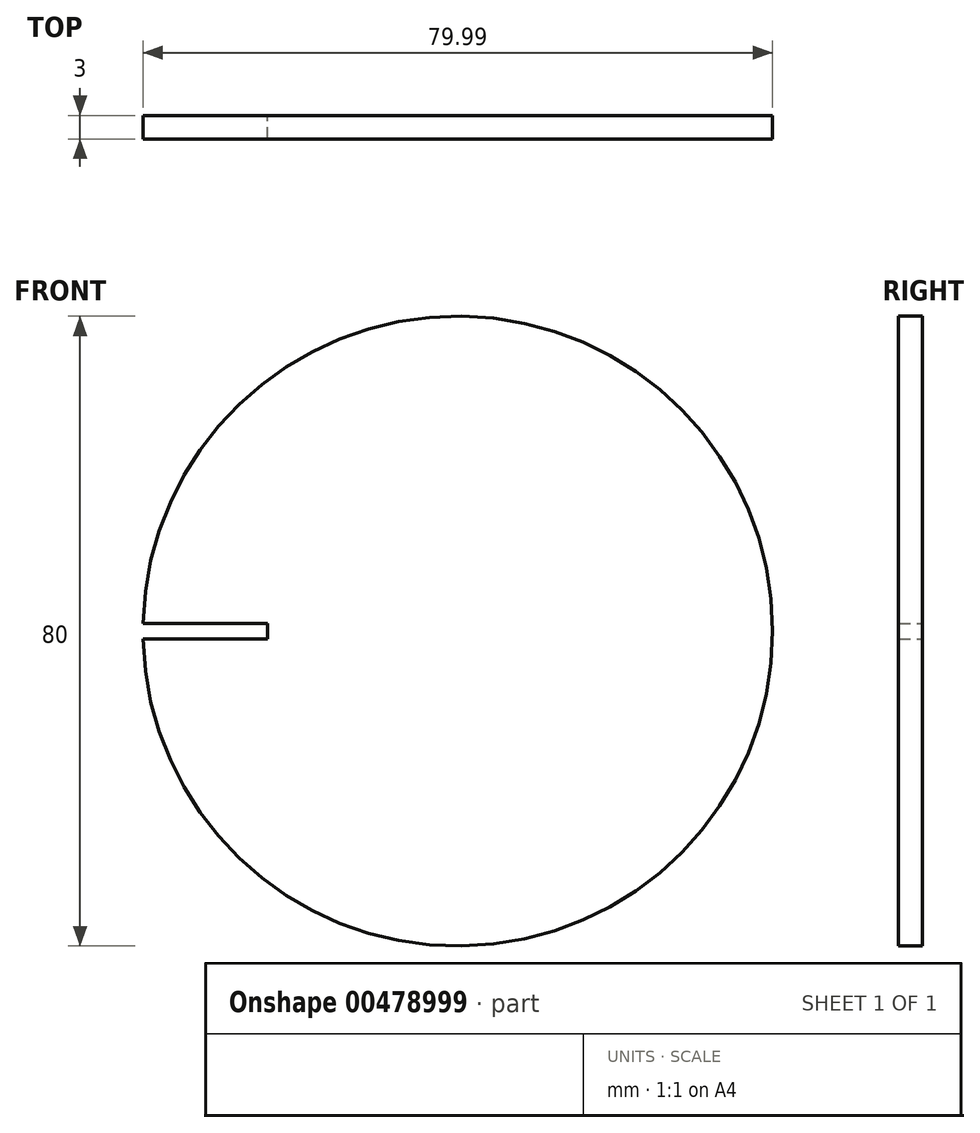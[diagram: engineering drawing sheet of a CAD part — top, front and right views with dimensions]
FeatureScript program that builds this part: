
annotation { "Feature Type Name" : "Feature", "Feature Type Description" : "" }
export const myFeature = defineFeature(function(context is Context, id is Id, definition is map)
    precondition{}
    {
        {
            var Q0;
            Q0=qCreatedBy(makeId("Front.planeOp"),FACE);
            var sketch = newSketch(context, id + "F0", { "sketchPlane" : qUnion([Q0])});
            skCircle(sketch, "E0", {"center": v(0, 0) * mm, "radius": 40 * mm});
            skSolve(sketch);
        }
        {
            var Q0;
            Q0=makeQuery(id+"F0.imprint","IMPRINT",FACE,{"disambiguationData":[TD([[makeQuery(id+"F0.imprint","IMPRINT",EDGE,{"derivedFrom":sQuery(id+"F0.wireOp",EDGE,"E0")}),1.0]])]});
            extrude(context, id + "F1", {"entities" : qUnion([Q0]), "depth" : 3 * mm});
        }
        {
            var Q0;
            Q0=qCreatedBy(makeId("Front.planeOp"),FACE);
            var sketch = newSketch(context, id + "F2", { "sketchPlane" : qUnion([Q0])});
            skLineSegment(sketch, "E1.bottom", {"start": v(-24.17, 1) * mm, "end": v(-57.33, 1) * mm});
            skLineSegment(sketch, "E1.top", {"start": v(-24.17, 0) * mm, "end": v(-57.33, 0) * mm});
            skLineSegment(sketch, "E1.left", {"start": v(-24.17, 1) * mm, "end": v(-24.17, 0) * mm});
            skLineSegment(sketch, "E1.right", {"start": v(-57.33, 1) * mm, "end": v(-57.33, 0) * mm});
            skLineSegment(sketch, "E2.MirrorCS", {"start": v(-24.17, -1) * mm, "end": v(-24.17, 0) * mm});
            skLineSegment(sketch, "E3.MirrorCS", {"start": v(-24.17, -1) * mm, "end": v(-57.33, -1) * mm});
            skLineSegment(sketch, "E4.MirrorCS", {"start": v(-57.33, -1) * mm, "end": v(-57.33, 0) * mm});
            skSolve(sketch);
        }
        {
            var Q0;
            Q0=makeQuery(id+"F2.imprint","IMPRINT",FACE,{"disambiguationData":[TD([[makeQuery(id+"F2.imprint","IMPRINT",EDGE,{"derivedFrom":sQuery(id+"F2.wireOp",EDGE,"E1.bottom")}),1.0]])]});
            extrude(context, id + "F3", {"entities" : qUnion([Q0]), "operationType" : NewBodyOperationType.REMOVE, "depth" : 24.9 * mm});
        }
        {
            var Q0;
            Q0=qSketchRegion(id+"F2",true);
            extrude(context, id + "F4", {"entities" : qUnion([Q0]), "operationType" : NewBodyOperationType.REMOVE, "depth" : 25 * mm});
        }
    });
